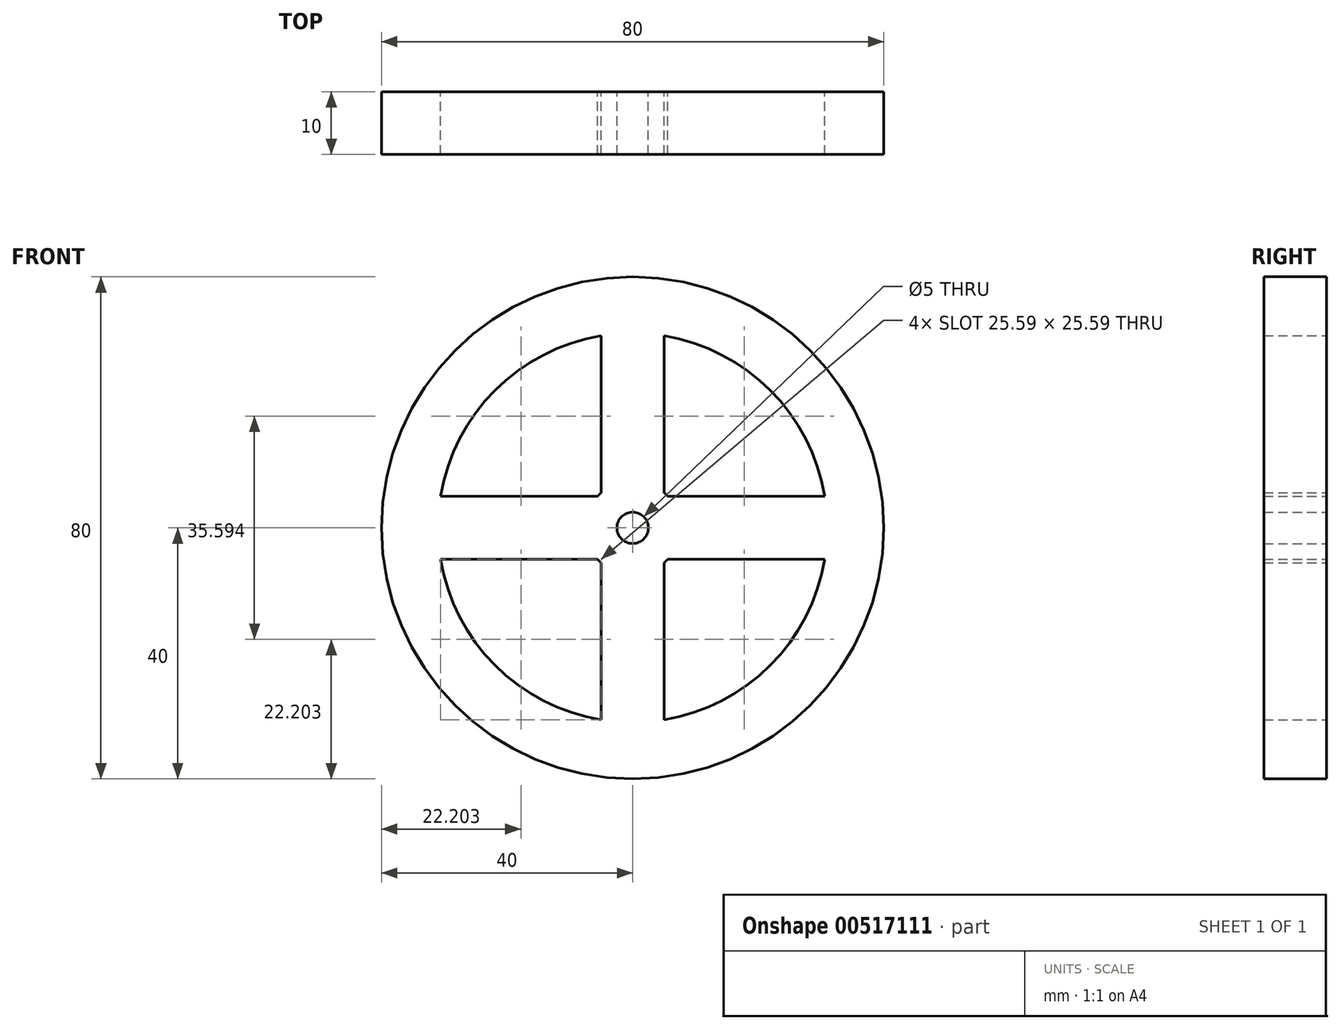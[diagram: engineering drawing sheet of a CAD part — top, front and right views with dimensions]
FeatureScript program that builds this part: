
annotation { "Feature Type Name" : "Feature", "Feature Type Description" : "" }
export const myFeature = defineFeature(function(context is Context, id is Id, definition is map)
    precondition{}
    {
        {
            var Q0;
            Q0=qCreatedBy(makeId("Front.planeOp"),FACE);
            var sketch = newSketch(context, id + "F0", { "sketchPlane" : qUnion([Q0])});
            skArc(sketch, "E0", {"start": v(5.6, 5) * mm, "mid": v(5.3, 5.3) * mm, "end": v(5, 5.6) * mm});
            skArc(sketch, "E1", {"start": v(-5, 30.6) * mm, "mid": v(-21.92, 21.92) * mm, "end": v(-30.6, 5) * mm});
            skCircle(sketch, "E2", {"center": v(0, 0) * mm, "radius": 40 * mm});
            skCircle(sketch, "E3", {"center": v(0, 0) * mm, "radius": 2.5 * mm});
            skLineSegment(sketch, "E4.0", {"start": v(5, 5.6) * mm, "end": v(5, 30.6) * mm});
            skLineSegment(sketch, "E5.0", {"start": v(-5, 5.6) * mm, "end": v(-5, 30.6) * mm});
            skLineSegment(sketch, "E6.0", {"start": v(5.6, -5) * mm, "end": v(30.6, -5) * mm});
            skLineSegment(sketch, "E7.0", {"start": v(5.6, 5) * mm, "end": v(30.6, 5) * mm});
            skLineSegment(sketch, "E8.0", {"start": v(-5.6, 5) * mm, "end": v(-30.6, 5) * mm});
            skLineSegment(sketch, "E9.0", {"start": v(-5.6, -5) * mm, "end": v(-30.6, -5) * mm});
            skLineSegment(sketch, "E10.0", {"start": v(-5, -5.6) * mm, "end": v(-5, -30.6) * mm});
            skLineSegment(sketch, "E11.0", {"start": v(5, -5.6) * mm, "end": v(5, -30.6) * mm});
            skArc(sketch, "E12.trimOffspring", {"start": v(-5, 5.6) * mm, "mid": v(-5.3, 5.3) * mm, "end": v(-5.6, 5) * mm});
            skArc(sketch, "E13.trimOffspring", {"start": v(5, -5.6) * mm, "mid": v(5.3, -5.3) * mm, "end": v(5.6, -5) * mm});
            skArc(sketch, "E14.trimOffspring", {"start": v(-5.6, -5) * mm, "mid": v(-5.3, -5.3) * mm, "end": v(-5, -5.6) * mm});
            skArc(sketch, "E15.trimOffspring", {"start": v(30.6, 5) * mm, "mid": v(21.92, 21.92) * mm, "end": v(5, 30.6) * mm});
            skArc(sketch, "E16.trimOffspring", {"start": v(5, -30.6) * mm, "mid": v(21.92, -21.92) * mm, "end": v(30.6, -5) * mm});
            skArc(sketch, "E17.trimOffspring", {"start": v(-30.6, -5) * mm, "mid": v(-21.92, -21.92) * mm, "end": v(-5, -30.6) * mm});
            skLineSegment(sketch, "E18", {"start": v(0, 0) * mm, "end": v(2.5, 0) * mm});
            skSolve(sketch);
        }
        {
            var Q0;
            Q0 = qSketchRegion(id + "F0", true);
            extrude(context, id + "F1", {"entities" : qUnion([Q0]), "depth" : 10 * mm, "offsetDistance" : 25 * mm});
        }
    });
